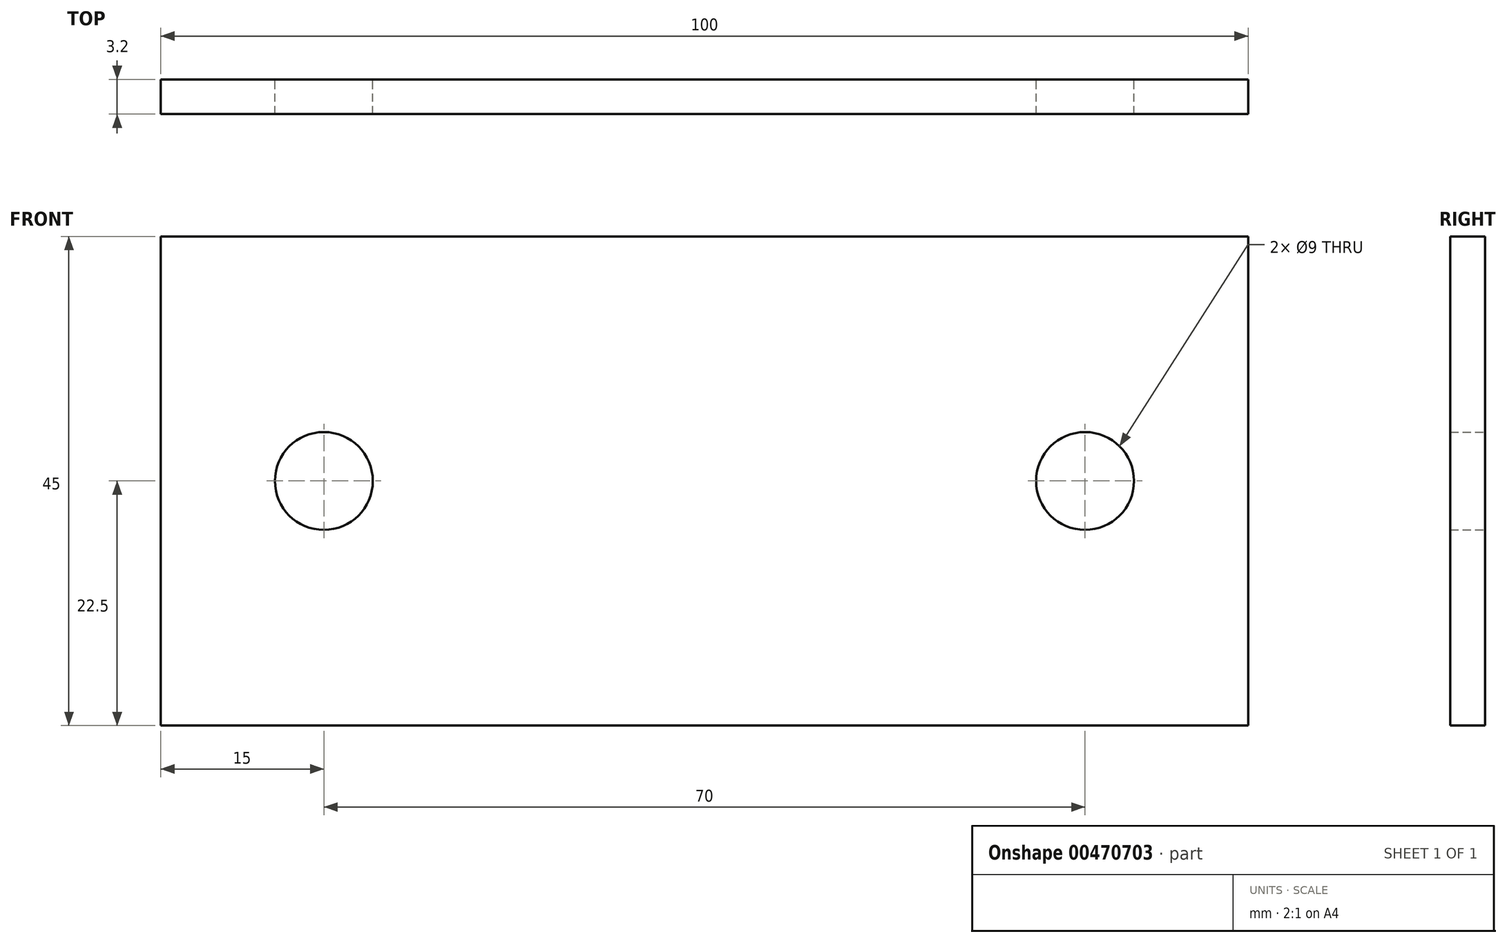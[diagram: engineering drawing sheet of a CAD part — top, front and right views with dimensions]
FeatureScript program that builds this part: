
annotation { "Feature Type Name" : "Feature", "Feature Type Description" : "" }
export const myFeature = defineFeature(function(context is Context, id is Id, definition is map)
    precondition{}
    {
        {
            var Q0;
            Q0=qCreatedBy(makeId("Front.planeOp"),FACE);
            var sketch = newSketch(context, id + "F0", { "sketchPlane" : qUnion([Q0])});
            skLineSegment(sketch, "E0.bottom", {"start": v(-50, 22.5) * mm, "end": v(50, 22.5) * mm});
            skLineSegment(sketch, "E0.top", {"start": v(-50, -22.5) * mm, "end": v(50, -22.5) * mm});
            skLineSegment(sketch, "E0.left", {"start": v(-50, 22.5) * mm, "end": v(-50, -22.5) * mm});
            skLineSegment(sketch, "E0.right", {"start": v(50, 22.5) * mm, "end": v(50, -22.5) * mm});
            skPoint(sketch, "E0.middle", {"position": v(0, 0) * mm});
            skLineSegment(sketch, "E1", {"start": v(-20, 22.5) * mm, "end": v(-20, -22.5) * mm, "construction": true});
            skLineSegment(sketch, "E2", {"start": v(20, 22.5) * mm, "end": v(20, -22.5) * mm, "construction": true});
            skLineSegment(sketch, "E3", {"start": v(-35, 22.5) * mm, "end": v(-35, -22.5) * mm, "construction": true});
            skLineSegment(sketch, "E4", {"start": v(35, 23.8) * mm, "end": v(35, -22.5) * mm, "construction": true});
            skLineSegment(sketch, "E5", {"start": v(-50, 0) * mm, "end": v(50, 0) * mm, "construction": true});
            skCircle(sketch, "E6", {"center": v(-35, 0) * mm, "radius": 4.5 * mm});
            skCircle(sketch, "E7", {"center": v(35, 0) * mm, "radius": 4.5 * mm});
            skSolve(sketch);
        }
        {
            var Q0;
            Q0 = qSketchRegion(id + "F0", true);
            extrude(context, id + "F1", {"entities" : qUnion([Q0]), "depth" : 3.2 * mm});
        }
    });
